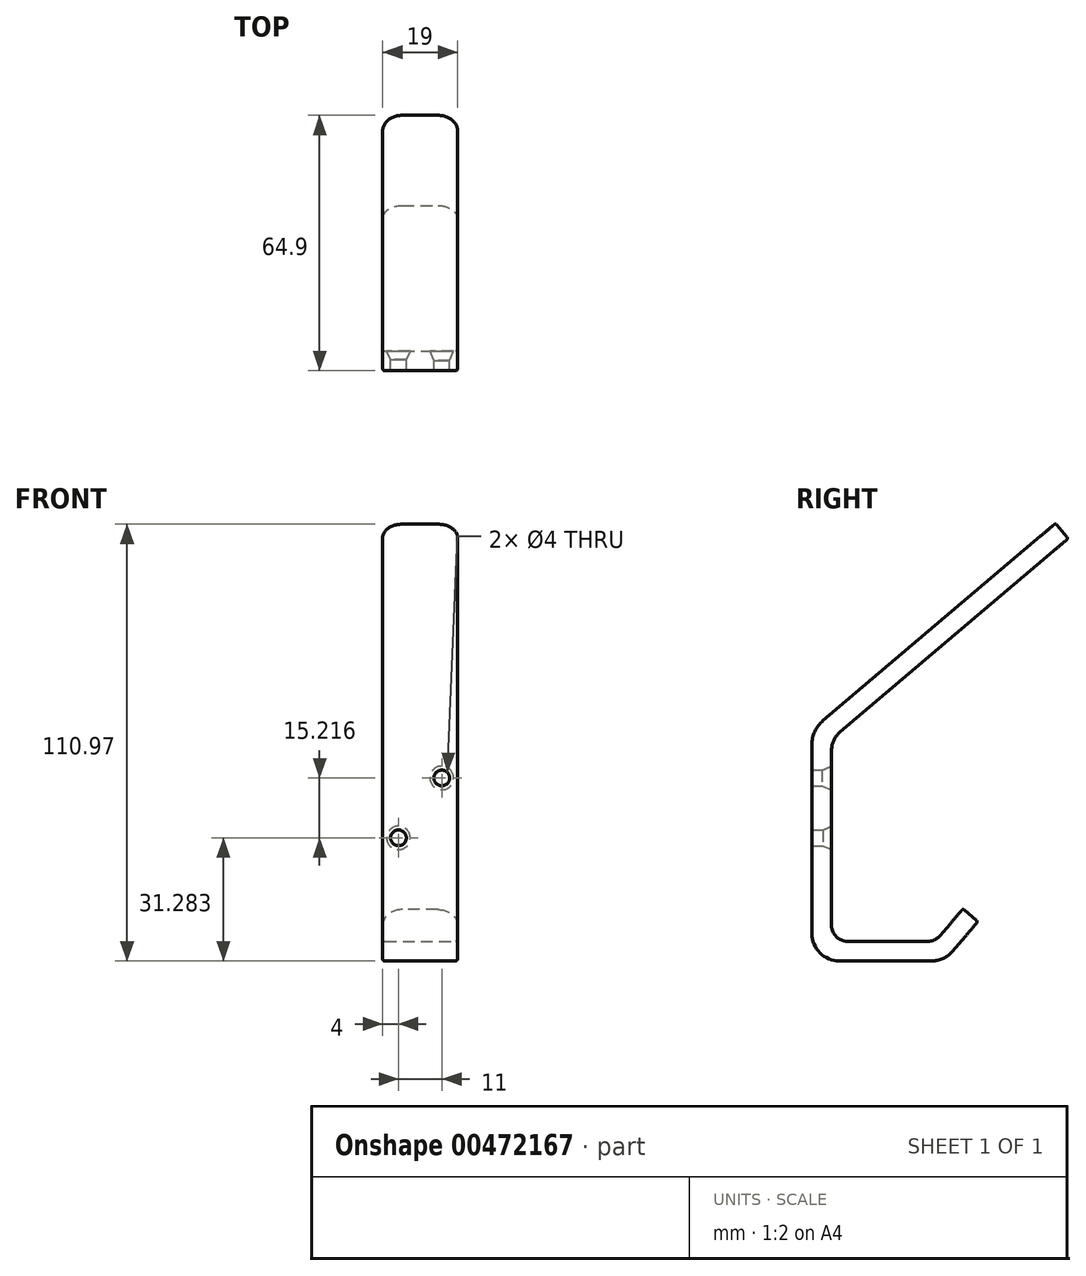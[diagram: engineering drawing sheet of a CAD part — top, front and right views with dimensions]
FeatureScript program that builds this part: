
annotation { "Feature Type Name" : "Feature", "Feature Type Description" : "" }
export const myFeature = defineFeature(function(context is Context, id is Id, definition is map)
    precondition{}
    {
        {
            var Q0;
            Q0=qCreatedBy(makeId("Right.planeOp"),FACE);
            var sketch = newSketch(context, id + "F0", { "sketchPlane" : qUnion([Q0])});
            skLineSegment(sketch, "E0", {"start": v(0, 0) * mm, "end": v(0, 2.5) * mm});
            skLineSegment(sketch, "E1", {"start": v(37.77, 9.14) * mm, "end": v(35.87, 10.76) * mm});
            skLineSegment(sketch, "E2", {"start": v(35.87, 10.76) * mm, "end": v(28.84, 2.5) * mm});
            skLineSegment(sketch, "E3", {"start": v(0, -2.5) * mm, "end": v(31.16, -2.5) * mm});
            skLineSegment(sketch, "E4", {"start": v(37.77, 9.14) * mm, "end": v(39.68, 7.52) * mm});
            skLineSegment(sketch, "E5", {"start": v(39.68, 7.52) * mm, "end": v(31.16, -2.5) * mm});
            skLineSegment(sketch, "E6", {"start": v(2.5, 2.5) * mm, "end": v(28.84, 2.5) * mm});
            skLineSegment(sketch, "E7", {"start": v(0, -2.5) * mm, "end": v(-2.5, -2.5) * mm});
            skLineSegment(sketch, "E8", {"start": v(-2.5, -2.5) * mm, "end": v(-2.5, 56.16) * mm});
            skLineSegment(sketch, "E9", {"start": v(2.5, 53.84) * mm, "end": v(2.5, 2.5) * mm});
            skLineSegment(sketch, "E10", {"start": v(60.99, 106.77) * mm, "end": v(62.6, 104.87) * mm});
            skLineSegment(sketch, "E11", {"start": v(60.99, 106.77) * mm, "end": v(59.37, 108.68) * mm});
            skLineSegment(sketch, "E12", {"start": v(59.37, 108.68) * mm, "end": v(-2.5, 56.16) * mm});
            skLineSegment(sketch, "E13", {"start": v(62.6, 104.87) * mm, "end": v(2.5, 53.84) * mm});
            skSolve(sketch);
        }
        {
            var Q0;
            Q0=makeQuery(id+"F0.imprint","IMPRINT",FACE,{"disambiguationData":[TD([[makeQuery(id+"F0.imprint","IMPRINT",EDGE,{"derivedFrom":sQuery(id+"F0.wireOp",EDGE,"E1")}),1.0]])]});
            extrude(context, id + "F1", {"entities" : qUnion([Q0]), "oppositeDirection" : true, "depth" : 19 * mm});
        }
        {
            var Q0;
            Q0=makeQuery(id+"F1.opExtrude","SWEPT_EDGE",EDGE,{"disambiguationData":[OSD([sQuery(id+"F0.wireOp",EDGE,"E8"),sQuery(id+"F0.wireOp",EDGE,"E12")])]});
            fillet(context, id + "F2", {"entities" : qUnion([Q0]), "radius" : 8 * mm, "tangentPropagation" : true, "allowEdgeOverflow" : false});
        }
        {
            var Q0;
            Q0=makeQuery(id+"F1.opExtrude","SWEPT_EDGE",EDGE,{"disambiguationData":[OSD([sQuery(id+"F0.wireOp",EDGE,"E9"),sQuery(id+"F0.wireOp",EDGE,"E13")])]});
            fillet(context, id + "F3", {"entities" : qUnion([Q0]), "radius" : 6 * mm, "tangentPropagation" : true, "allowEdgeOverflow" : false});
        }
        {
            var Q0;
            Q0=makeQuery(id+"F1.opExtrude","SWEPT_EDGE",EDGE,{"disambiguationData":[OSD([sQuery(id+"F0.wireOp",EDGE,"E7"),sQuery(id+"F0.wireOp",EDGE,"E8")])]});
            fillet(context, id + "F4", {"entities" : qUnion([Q0]), "radius" : 7 * mm, "tangentPropagation" : true, "allowEdgeOverflow" : false});
        }
        {
            var Q0;
            Q0=makeQuery(id+"F1.opExtrude","SWEPT_EDGE",EDGE,{"disambiguationData":[OSD([sQuery(id+"F0.wireOp",EDGE,"E6"),sQuery(id+"F0.wireOp",EDGE,"E9")])]});
            fillet(context, id + "F5", {"entities" : qUnion([Q0]), "radius" : 4 * mm, "tangentPropagation" : true, "allowEdgeOverflow" : false});
        }
        {
            var Q0;
            Q0=makeQuery(id+"F1.opExtrude","SWEPT_EDGE",EDGE,{"disambiguationData":[OSD([sQuery(id+"F0.wireOp",EDGE,"E3"),sQuery(id+"F0.wireOp",EDGE,"E5")])]});
            fillet(context, id + "F6", {"entities" : qUnion([Q0]), "radius" : 7 * mm, "tangentPropagation" : true, "allowEdgeOverflow" : false});
        }
        {
            var Q0;
            Q0=makeQuery(id+"F1.opExtrude","SWEPT_EDGE",EDGE,{"disambiguationData":[OSD([sQuery(id+"F0.wireOp",EDGE,"E2"),sQuery(id+"F0.wireOp",EDGE,"E6")])]});
            fillet(context, id + "F7", {"entities" : qUnion([Q0]), "radius" : 4 * mm, "tangentPropagation" : true, "allowEdgeOverflow" : false});
        }
        {
            var Q0;
            Q0=makeQuery(id+"F1.opExtrude","CAP_EDGE",EDGE,{"disambiguationData":[OSD([sQuery(id+"F0.wireOp",EDGE,"E10"),sQuery(id+"F0.wireOp",EDGE,"E11")])],"isStart":true});
            fillet(context, id + "F8", {"entities" : qUnion([Q0]), "radius" : 5 * mm, "tangentPropagation" : true, "allowEdgeOverflow" : false});
        }
        {
            var Q0;
            Q0=makeQuery(id+"F1.opExtrude","CAP_EDGE",EDGE,{"disambiguationData":[OSD([sQuery(id+"F0.wireOp",EDGE,"E10"),sQuery(id+"F0.wireOp",EDGE,"E11")])],"isStart":false});
            fillet(context, id + "F9", {"entities" : qUnion([Q0]), "radius" : 5 * mm, "tangentPropagation" : true, "allowEdgeOverflow" : false});
        }
        {
            var Q0;
            Q0=makeQuery(id+"F1.opExtrude","CAP_EDGE",EDGE,{"disambiguationData":[OSD([sQuery(id+"F0.wireOp",EDGE,"E1"),sQuery(id+"F0.wireOp",EDGE,"E4")])],"isStart":false});
            fillet(context, id + "F10", {"entities" : qUnion([Q0]), "radius" : 5 * mm, "tangentPropagation" : true, "allowEdgeOverflow" : false});
        }
        {
            var Q0;
            Q0=makeQuery(id+"F1.opExtrude","CAP_EDGE",EDGE,{"disambiguationData":[OSD([sQuery(id+"F0.wireOp",EDGE,"E1"),sQuery(id+"F0.wireOp",EDGE,"E4")])],"isStart":true});
            fillet(context, id + "F11", {"entities" : qUnion([Q0]), "radius" : 5 * mm, "tangentPropagation" : true, "allowEdgeOverflow" : false});
        }
        {
            var Q0;
            Q0=makeQuery(id+"F1.opExtrude","SWEPT_FACE",FACE,{"disambiguationData":[OSD([sQuery(id+"F0.wireOp",EDGE,"E9")])]});
            var sketch = newSketch(context, id + "F12", { "sketchPlane" : qUnion([Q0])});
            skLineSegment(sketch, "E14", {"start": v(0, 44) * mm, "end": v(4, 44) * mm});
            skLineSegment(sketch, "E15", {"start": v(19, 30.02) * mm, "end": v(15, 30.02) * mm});
            skCircle(sketch, "E16", {"center": v(4, 44) * mm, "radius": 3 * mm});
            skPoint(sketch, "E17", {"position": v(15, 30.02) * mm});
            skSolve(sketch);
        }
        {
            var Q0;
            Q0=sQuery(id+"F12.wireOp",VERTEX,"E16.center");
            var Q1;
            Q1=makeQuery(id+"F1.opExtrude","SWEPT_BODY",BODY,{"disambiguationData":[OSD([sQuery(id+"F0.wireOp",EDGE,"E1"),sQuery(id+"F0.wireOp",EDGE,"E2"),sQuery(id+"F0.wireOp",EDGE,"E3"),sQuery(id+"F0.wireOp",EDGE,"E4"),sQuery(id+"F0.wireOp",EDGE,"E5"),sQuery(id+"F0.wireOp",EDGE,"E6"),sQuery(id+"F0.wireOp",EDGE,"E7"),sQuery(id+"F0.wireOp",EDGE,"E8"),sQuery(id+"F0.wireOp",EDGE,"E9"),sQuery(id+"F0.wireOp",EDGE,"E10"),sQuery(id+"F0.wireOp",EDGE,"E11"),sQuery(id+"F0.wireOp",EDGE,"E12"),sQuery(id+"F0.wireOp",EDGE,"E13")])]});
            hole(context, id + "F13", {"style" : HoleStyle.C_SINK, "endStyle" : HoleEndStyle.THROUGH, "holeDiameter" : 4 * mm, "cSinkDiameter" : 6 * mm, "cSinkAngle" : 45 * degree, "isTappedThrough" : true, "tappedDepth" : 12 * mm, "tapClearance" : 3, "startFromSketch" : true, "locations" : qUnion([Q0]), "scope" : qUnion([Q1])});
        }
        {
            var Q0;
            Q0=makeQuery(id+"F1.opExtrude","SWEPT_FACE",FACE,{"disambiguationData":[OSD([sQuery(id+"F0.wireOp",EDGE,"E9")])]});
            var sketch = newSketch(context, id + "F14", { "sketchPlane" : qUnion([Q0])});
            skLineSegment(sketch, "E18", {"start": v(19, 28.78) * mm, "end": v(15, 28.78) * mm});
            skPoint(sketch, "E18.endSnap0", {"position": v(19, 28.78) * mm});
            skPoint(sketch, "E19", {"position": v(15, 28.78) * mm});
            skSolve(sketch);
        }
        {
            var Q0;
            Q0=sQuery(id+"F14.wireOp",VERTEX,"E19");
            var Q1;
            Q1=makeQuery(id+"F1.opExtrude","SWEPT_BODY",BODY,{"disambiguationData":[OSD([sQuery(id+"F0.wireOp",EDGE,"E1"),sQuery(id+"F0.wireOp",EDGE,"E2"),sQuery(id+"F0.wireOp",EDGE,"E3"),sQuery(id+"F0.wireOp",EDGE,"E4"),sQuery(id+"F0.wireOp",EDGE,"E5"),sQuery(id+"F0.wireOp",EDGE,"E6"),sQuery(id+"F0.wireOp",EDGE,"E7"),sQuery(id+"F0.wireOp",EDGE,"E8"),sQuery(id+"F0.wireOp",EDGE,"E9"),sQuery(id+"F0.wireOp",EDGE,"E10"),sQuery(id+"F0.wireOp",EDGE,"E11"),sQuery(id+"F0.wireOp",EDGE,"E12"),sQuery(id+"F0.wireOp",EDGE,"E13")])]});
            hole(context, id + "F15", {"style" : HoleStyle.C_SINK, "endStyle" : HoleEndStyle.THROUGH, "holeDiameter" : 4 * mm, "cSinkDiameter" : 6 * mm, "cSinkAngle" : 50 * degree, "isTappedThrough" : true, "tappedDepth" : 12 * mm, "tapClearance" : 3, "startFromSketch" : true, "locations" : qUnion([Q0]), "scope" : qUnion([Q1])});
        }
        {
            var Q0;
            Q0=makeQuery(id+"F1.opExtrude","CAP_EDGE",EDGE,{"disambiguationData":[OSD([sQuery(id+"F0.wireOp",EDGE,"E12")])],"isStart":true});
            fillet(context, id + "F16", {"entities" : qUnion([Q0]), "radius" : 0.5 * mm, "tangentPropagation" : true, "allowEdgeOverflow" : false});
        }
        {
            var Q0;
            Q0=makeQuery(id+"F1.opExtrude","CAP_EDGE",EDGE,{"disambiguationData":[OSD([sQuery(id+"F0.wireOp",EDGE,"E13")])],"isStart":true});
            fillet(context, id + "F17", {"entities" : qUnion([Q0]), "radius" : 0.5 * mm, "tangentPropagation" : true, "allowEdgeOverflow" : false});
        }
    });
